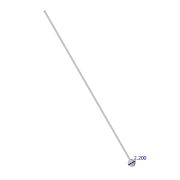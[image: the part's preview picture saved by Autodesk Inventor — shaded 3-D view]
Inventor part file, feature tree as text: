
AUTODESK INVENTOR PART (.ipt)
format: ipt  version: 2018.3 (Build 223284000, 284)  size: 161,792 bytes
history: native  units: in
note: dims shown in document units (in); Inventor stores cm internally (conversion verified against a paired STEP export)
features: sketch x2, revolve x1, other x1
ambient origin geometry x8: Origin, YZ Plane, XZ Plane, XY Plane, X Axis, Y Axis, Z Axis, Center Point
bodies: Solid1 (feature_tree), Solid2 (feature_tree)
feature tree (4):
  revolve  "Revolution1"  [1 undecoded]
  sketch  "Sketch2"  dims[d2=90.0deg d3=2.2in]
  other  "Form1"
  sketch  "Sketch1"  dims[d0=48.0in d1=0.25in]
note: 1 required parameter value undecoded (feature->parameter linkage not recoverable at this tier; creation-order binding heuristic only, values carry confidence <= 0.55)
